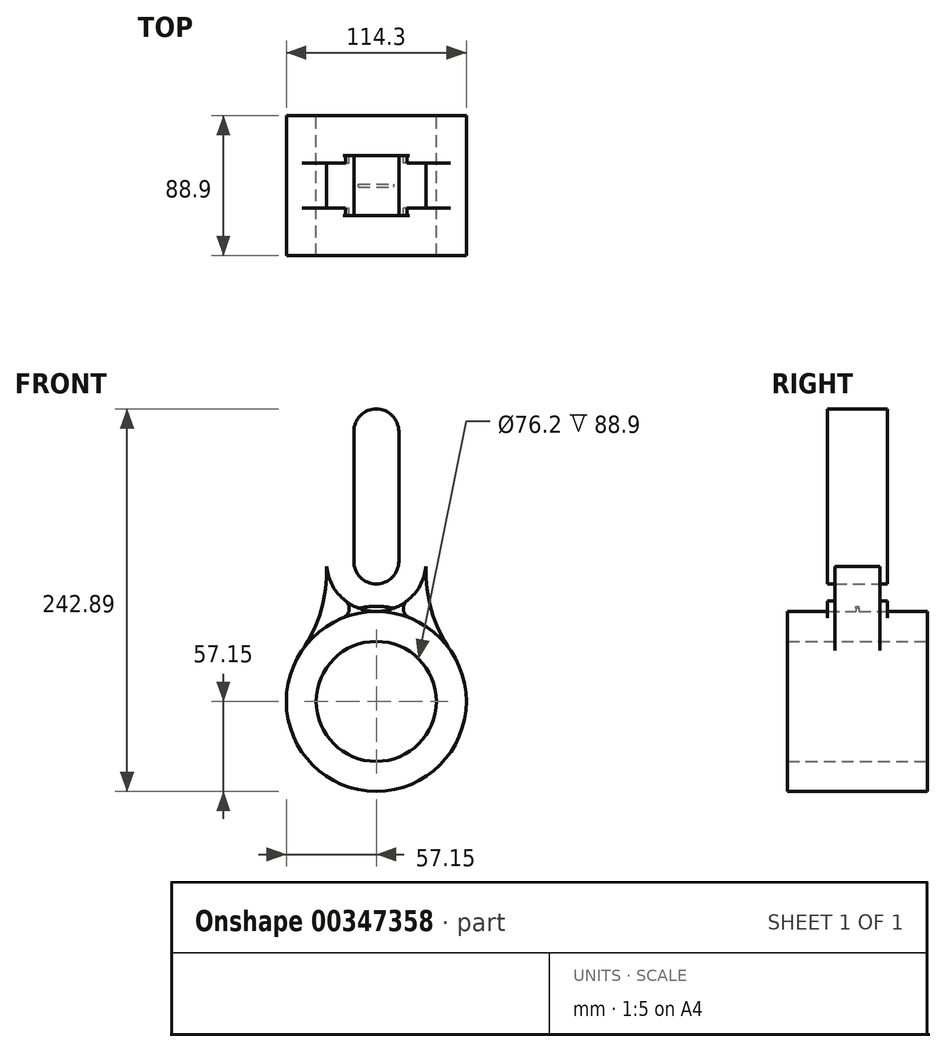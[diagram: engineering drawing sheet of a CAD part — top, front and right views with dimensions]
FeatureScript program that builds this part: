
annotation { "Feature Type Name" : "Feature", "Feature Type Description" : "" }
export const myFeature = defineFeature(function(context is Context, id is Id, definition is map)
    precondition{}
    {
        {
            var Q0;
            Q0=qCreatedBy(makeId("Front.planeOp"),FACE);
            var sketch = newSketch(context, id + "F0", { "sketchPlane" : qUnion([Q0])});
            skCircle(sketch, "E0", {"center": v(0, 0) * mm, "radius": 38.1 * mm});
            skCircle(sketch, "E1", {"center": v(0, 0) * mm, "radius": 57.15 * mm});
            skSolve(sketch);
        }
        {
            var Q0;
            Q0=makeQuery(id+"F0.imprint","IMPRINT",FACE,{"disambiguationData":[TD([[makeQuery(id+"F0.imprint","IMPRINT",EDGE,{"derivedFrom":sQuery(id+"F0.wireOp",EDGE,"E0")}),-1.0]])]});
            extrude(context, id + "F1", {"entities" : qUnion([Q0]), "depth" : 88.9 * mm, "symmetric" : true});
        }
        {
            var Q0;
            Q0=qCreatedBy(makeId("Front.planeOp"),FACE);
            var sketch = newSketch(context, id + "F2", { "sketchPlane" : qUnion([Q0])});
            skLineSegment(sketch, "E2", {"start": v(0, 88.9) * mm, "end": v(0, 171.45) * mm});
            skArc(sketch, "E3.0.startCap", {"start": v(14.29, 88.9) * mm, "mid": v(0, 74.61) * mm, "end": v(-14.29, 88.9) * mm});
            skArc(sketch, "E3.0.endCap", {"start": v(-14.29, 171.45) * mm, "mid": v(0, 185.74) * mm, "end": v(14.29, 171.45) * mm});
            skLineSegment(sketch, "E3.0.left", {"start": v(-14.29, 88.9) * mm, "end": v(-14.29, 171.45) * mm});
            skLineSegment(sketch, "E3.0.right", {"start": v(14.29, 88.9) * mm, "end": v(14.29, 171.45) * mm});
            skArc(sketch, "E4.0.startCap", {"start": v(31.75, 88.9) * mm, "mid": v(0, 57.15) * mm, "end": v(-31.75, 88.9) * mm});
            skArc(sketch, "E4.0.endCap", {"start": v(-31.75, 171.45) * mm, "mid": v(0, 203.2) * mm, "end": v(31.75, 171.45) * mm});
            skLineSegment(sketch, "E4.0.left", {"start": v(-31.75, 88.9) * mm, "end": v(-31.75, 171.45) * mm});
            skLineSegment(sketch, "E4.0.right", {"start": v(31.75, 88.9) * mm, "end": v(31.75, 171.45) * mm});
            skCircle(sketch, "E5.0", {"center": v(0, 0) * mm, "radius": 57.15 * mm});
            skArc(sketch, "E6", {"start": v(19.64, 63.95) * mm, "mid": v(17.28, 58.06) * mm, "end": v(21.21, 53.07) * mm});
            skArc(sketch, "E7", {"start": v(-21.21, 53.07) * mm, "mid": v(-17.28, 58.06) * mm, "end": v(-19.64, 63.95) * mm});
            skSolve(sketch);
        }
        {
            var Q0;
            Q0=makeQuery(id+"F2.imprint","IMPRINT",FACE,{"disambiguationData":[TD([[makeQuery(id+"F2.imprint","IMPRINT",EDGE,{"derivedFrom":sQuery(id+"F2.wireOp",EDGE,"E3.0.startCap")}),1.0]])]});
            var Q1;
            {var subQ0=sQuery(id+"F2.wireOp",EDGE,"E7");Q1=makeQuery(id+"F2.imprint","IMPRINT",FACE,{"disambiguationData":[TD([[makeQuery(id+"F2.imprint","IMPRINT",EDGE,{"derivedFrom":subQ0}),-1.0]])]});}
            var Q2;
            {var subQ0=sQuery(id+"F2.wireOp",EDGE,"E6");Q2=makeQuery(id+"F2.imprint","IMPRINT",FACE,{"disambiguationData":[TD([[makeQuery(id+"F2.imprint","IMPRINT",EDGE,{"derivedFrom":subQ0}),-1.0]])]});}
            extrude(context, id + "F3", {"entities" : qUnion([Q0, Q1, Q2]), "operationType" : NewBodyOperationType.ADD, "depth" : 38.1 * mm, "symmetric" : true});
        }
        {
            var Q0;
            Q0=qCreatedBy(makeId("Front.planeOp"),FACE);
            var sketch = newSketch(context, id + "F4", { "sketchPlane" : qUnion([Q0])});
            skLineSegment(sketch, "E8.0", {"start": v(31.75, 88.9) * mm, "end": v(31.75, 171.45) * mm});
            skCircle(sketch, "E9.0", {"center": v(0, 0) * mm, "radius": 57.15 * mm});
            skLineSegment(sketch, "E10.0", {"start": v(-31.75, 88.9) * mm, "end": v(-31.75, 171.45) * mm});
            skArc(sketch, "E11", {"start": v(31.75, 88.9) * mm, "mid": v(34.64, 59.31) * mm, "end": v(47.12, 32.33) * mm});
            skArc(sketch, "E12", {"start": v(-47.12, 32.33) * mm, "mid": v(-34.64, 59.31) * mm, "end": v(-31.75, 88.9) * mm});
            skArc(sketch, "E13.0", {"start": v(-21.21, 53.07) * mm, "mid": v(-17.28, 58.06) * mm, "end": v(-19.64, 63.95) * mm});
            skArc(sketch, "E14.0", {"start": v(-19.64, 63.95) * mm, "mid": v(-28.56, 75.03) * mm, "end": v(-31.75, 88.9) * mm});
            skArc(sketch, "E15.0", {"start": v(31.75, 88.9) * mm, "mid": v(28.56, 75.03) * mm, "end": v(19.64, 63.95) * mm});
            skArc(sketch, "E16.0", {"start": v(19.64, 63.95) * mm, "mid": v(17.28, 58.06) * mm, "end": v(21.21, 53.07) * mm});
            skSolve(sketch);
        }
        {
            var Q0;
            {var subQ3=sQuery(id+"F4.wireOp",EDGE,"E13.0");Q0=makeQuery(id+"F4.imprint","IMPRINT",FACE,{"disambiguationData":[TD([[makeQuery(id+"F4.imprint","IMPRINT",EDGE,{"derivedFrom":subQ3}),1.0]])]});}
            var Q1;
            {var subQ0=sQuery(id+"F4.wireOp",EDGE,"E16.0");Q1=makeQuery(id+"F4.imprint","IMPRINT",FACE,{"disambiguationData":[TD([[makeQuery(id+"F4.imprint","IMPRINT",EDGE,{"derivedFrom":subQ0}),1.0]])]});}
            extrude(context, id + "F5", {"entities" : qUnion([Q0, Q1]), "operationType" : NewBodyOperationType.ADD, "depth" : 28.57 * mm, "symmetric" : true});
        }
        {
            var Q0;
            Q0=qCreatedBy(makeId("Front.planeOp"),FACE);
            var sketch = newSketch(context, id + "F6", { "sketchPlane" : qUnion([Q0])});
            skArc(sketch, "E17.0", {"start": v(-21.21, 53.07) * mm, "mid": v(-17.28, 58.06) * mm, "end": v(-19.64, 63.95) * mm});
            skArc(sketch, "E18.0", {"start": v(19.64, 63.95) * mm, "mid": v(17.28, 58.06) * mm, "end": v(21.21, 53.07) * mm});
            skArc(sketch, "E19", {"start": v(17.33, 57.78) * mm, "mid": v(0, 60.33) * mm, "end": v(-17.33, 57.78) * mm});
            skCircle(sketch, "E20.0", {"center": v(0, 0) * mm, "radius": 57.15 * mm});
            skSolve(sketch);
        }
        {
            var Q0;
            {var subQ5=sQuery(id+"F6.wireOp",EDGE,"E19");Q0=makeQuery(id+"F6.imprint","IMPRINT",FACE,{"disambiguationData":[TD([[makeQuery(id+"F6.imprint","IMPRINT",EDGE,{"derivedFrom":subQ5}),1.0]])]});}
            extrude(context, id + "F7", {"entities" : qUnion([Q0]), "operationType" : NewBodyOperationType.ADD, "depth" : (1 + 1 / 8 + 2 * (5 / 16)) * mm, "symmetric" : true});
        }
    });
